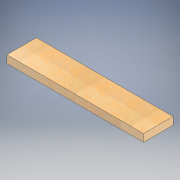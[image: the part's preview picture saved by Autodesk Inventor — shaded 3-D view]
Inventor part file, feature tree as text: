
AUTODESK INVENTOR PART (.ipt)
format: ipt  version: 2022.2 (Build 262287010, 287A)  size: 125,952 bytes
history: native  units: in
note: dims shown in document units (in); Inventor stores cm internally (conversion verified against a paired STEP export)
features: extrude x1, sketch x1
ambient origin geometry x8: Origin, YZ Plane, XZ Plane, XY Plane, X Axis, Y Axis, Z Axis, Center Point
bodies: Solid1 (feature_tree)
feature tree (2):
  extrude  "Extrusion1"  Depth=15.5in
  sketch  "Sketch1"  dims[d0=71.625in d1=15.5in d2=4.0in d3=0.0in]
